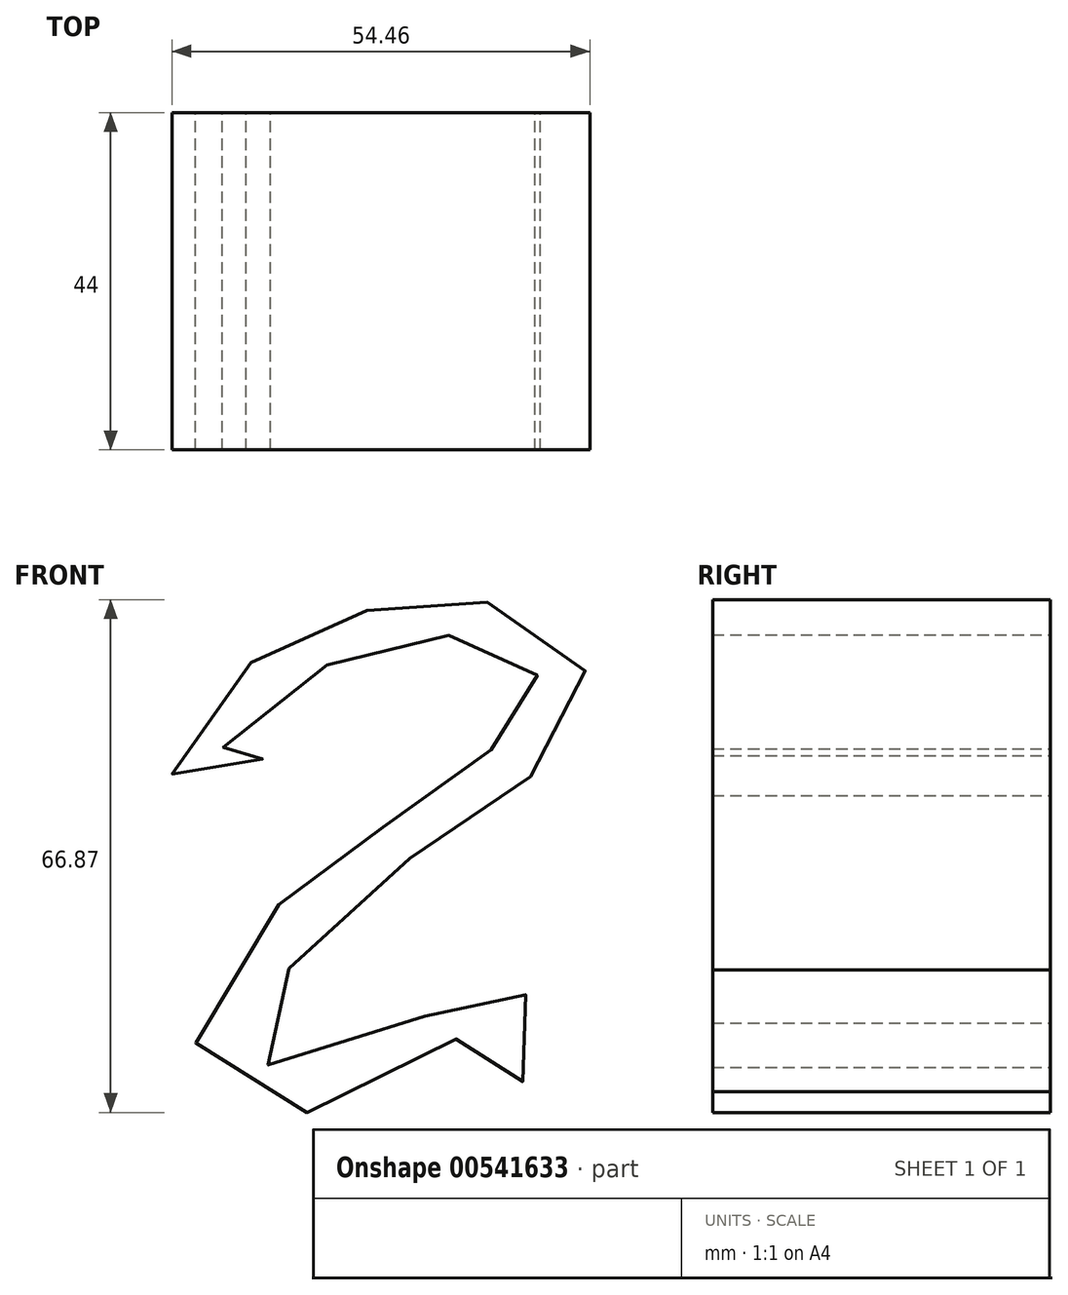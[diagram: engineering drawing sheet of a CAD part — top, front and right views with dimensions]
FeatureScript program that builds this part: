
annotation { "Feature Type Name" : "Feature", "Feature Type Description" : "" }
export const myFeature = defineFeature(function(context is Context, id is Id, definition is map)
    precondition{}
    {
        {
            var Q0;
            Q0=qCreatedBy(makeId("Front.planeOp"),FACE);
            var sketch = newSketch(context, id + "F0", { "sketchPlane" : qUnion([Q0])});
            skFitSpline(sketch, "E0", {"points": [v(0, 44.61) * mm, v(-14.73, 34.06) * mm, v(-28.87, 23.17) * mm, v(-37.76, 2.43) * mm, v(-12.97, 0) * mm, v(0, 8.65) * mm, v(5.1, 0) * mm, v(3.2, 15.08) * mm, v(-13.67, 6.64) * mm, v(-31.76, 5.4) * mm, v(-18.84, 23.63) * mm, v(-2.07, 36.17) * mm, v(12.7, 50.24) * mm, v(6.37, 61.49) * mm, v(-9.45, 63.95) * mm, v(-22.81, 60.43) * mm, v(-38.63, 48.83) * mm, v(-40.04, 38.63) * mm, v(-28.79, 44.61) * mm, v(-34.76, 43.9) * mm, v(-27.03, 52.34) * mm, v(-11.21, 58.67) * mm, v(2.5, 58.32) * mm, v(6.37, 51.64) * mm, v(0, 44.61) * mm]});
            skLineSegment(sketch, "E1", {"start": v(0, 74.8) * mm, "end": v(0, -31.47) * mm, "construction": true});
            skSolve(sketch);
        }
        {
            var Q0;
            Q0=makeQuery(id+"F0.imprint","IMPRINT",FACE,{"disambiguationData":[TD([[makeQuery(id+"F0.imprint","IMPRINT",EDGE,{"derivedFrom":sQuery(id+"F0.wireOp",EDGE,"E0")}),1.0]])]});
            extrude(context, id + "F1", {"entities" : qUnion([Q0]), "depth" : 44 * mm, "offsetDistance" : 25 * mm});
        }
    });
